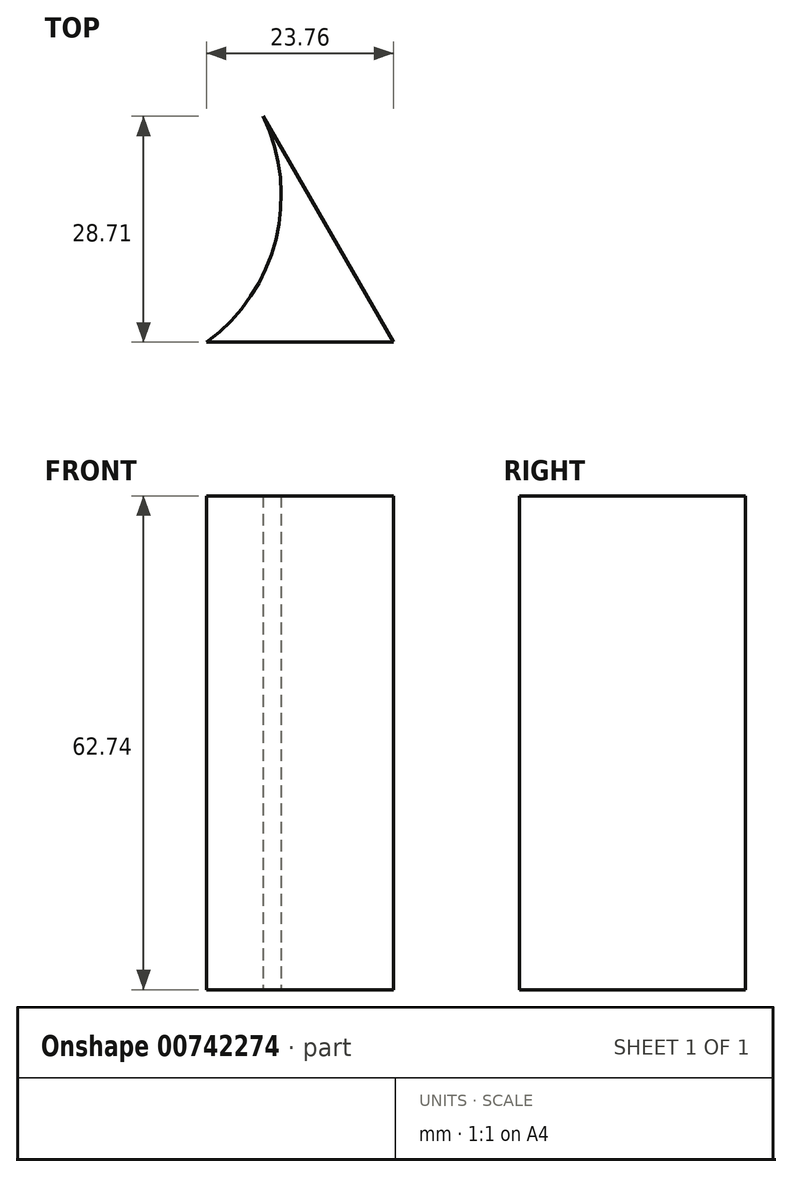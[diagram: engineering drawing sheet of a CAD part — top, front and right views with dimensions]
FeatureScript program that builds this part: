
annotation { "Feature Type Name" : "Feature", "Feature Type Description" : "" }
export const myFeature = defineFeature(function(context is Context, id is Id, definition is map)
    precondition{}
    {
        {
            var Q0;
            Q0=qCreatedBy(makeId("Top.planeOp"),FACE);
            var sketch = newSketch(context, id + "F0", { "sketchPlane" : qUnion([Q0])});
            skLineSegment(sketch, "E0", {"start": v(-43.85, 0) * mm, "end": v(0, 75.95) * mm});
            skLineSegment(sketch, "E1", {"start": v(-43.85, 0) * mm, "end": v(43.85, 0) * mm});
            skLineSegment(sketch, "E2", {"start": v(43.85, 0) * mm, "end": v(0, 75.95) * mm});
            skPoint(sketch, "E3", {"position": v(0, 0) * mm});
            skSolve(sketch);
        }
        {
            var Q0;
            Q0=makeQuery(id+"F0.imprint","IMPRINT",FACE,{"disambiguationData":[TD([[makeQuery(id+"F0.imprint","IMPRINT",EDGE,{"derivedFrom":sQuery(id+"F0.wireOp",EDGE,"E0")}),-1.0]])]});
            extrude(context, id + "F1", {"entities" : qUnion([Q0]), "depth" : 62.74 * mm, "offsetDistance" : 25.4 * mm});
        }
        {
            var Q0;
            Q0=makeQuery(id+"F1.opExtrude","CAP_FACE",FACE,{"disambiguationData":[OSD([sQuery(id+"F0.wireOp",EDGE,"E0"),sQuery(id+"F0.wireOp",EDGE,"E1"),sQuery(id+"F0.wireOp",EDGE,"E2")])],"isStart":true});
            var sketch = newSketch(context, id + "F2", { "sketchPlane" : qUnion([Q0])});
            skCircle(sketch, "E4", {"center": v(6.46, -18.67) * mm, "radius": 23.11 * mm});
            skSolve(sketch);
        }
        {
            var Q0;
            Q0 = qSketchRegion(id + "F2", true);
            extrude(context, id + "F3", {"entities" : qUnion([Q0]), "operationType" : NewBodyOperationType.REMOVE, "oppositeDirection" : true, "depth" : 71.12 * mm, "offsetDistance" : 25.4 * mm});
        }
        {
            var Q0;
            Q0=makeQuery(id+"F3.boolean.opBoolean","SPLIT",BODY,{"disambiguationData":[OD(1.0)],"derivedFrom":makeQuery(id+"F1.opExtrude","SWEPT_BODY",BODY,{"disambiguationData":[OSD([sQuery(id+"F0.wireOp",EDGE,"E0"),sQuery(id+"F0.wireOp",EDGE,"E1"),sQuery(id+"F0.wireOp",EDGE,"E2")])]})});
            deleteBodies(context, id + "F4", {"entities" : qUnion([Q0])});
        }
    });
